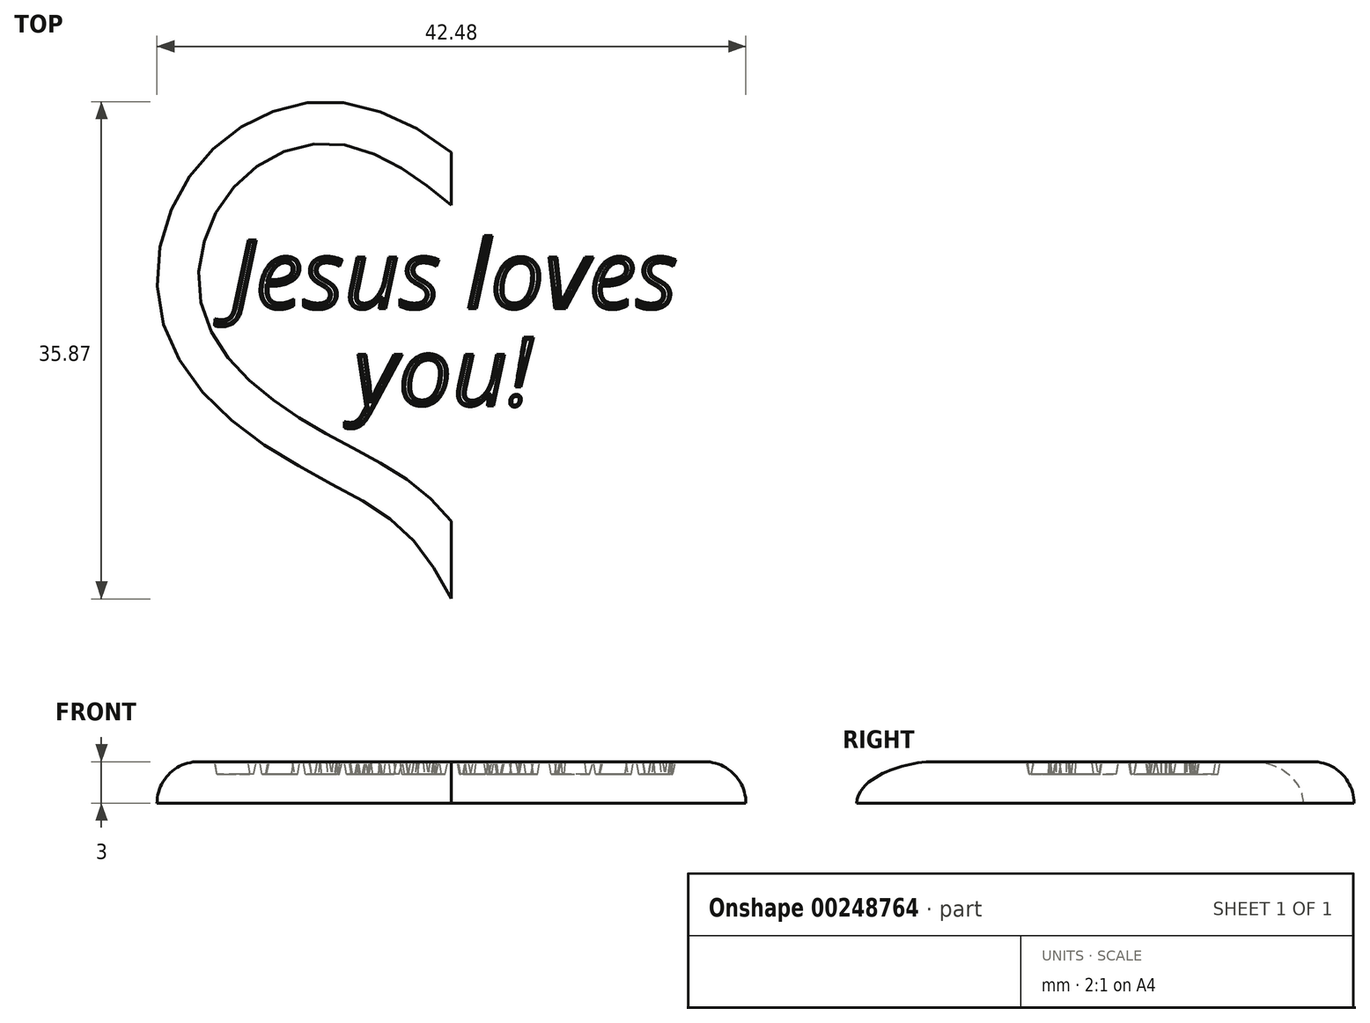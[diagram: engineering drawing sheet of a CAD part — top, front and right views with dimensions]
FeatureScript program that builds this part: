
annotation { "Feature Type Name" : "Feature", "Feature Type Description" : "" }
export const myFeature = defineFeature(function(context is Context, id is Id, definition is map)
    precondition{}
    {
        {
            var Q0;
            Q0=qCreatedBy(makeId("Top.planeOp"),FACE);
            var sketch = newSketch(context, id + "F0", { "sketchPlane" : qUnion([Q0])});
            skText(sketch, "E0", { "text": "Jesus loves", "fontName": "OpenSans-Italic.ttf"});
            skText(sketch, "E1", { "text": "you!", "fontName": "OpenSans-Italic.ttf"});
            const initialGuessF0  = {"E0": [-0.016, 0, 1, 0, 0.005], "E1": [-0.00706, -0.007, 1, 0, 0.005]};
            skSetInitialGuess(sketch, initialGuessF0);
            skSolve(sketch);
        }
        {
            var Q0;
            Q0=qCreatedBy(makeId("Top.planeOp"),FACE);
            var sketch = newSketch(context, id + "F1", { "sketchPlane" : qUnion([Q0])});
            skFitSpline(sketch, "E2", {"points": [v(0, 11.29) * mm, v(-8, 14.88) * mm, v(-14.74, 13.36) * mm, v(-19.74, 8.14) * mm, v(-21.05, 0) * mm, v(-16.7, -7.3) * mm, v(-9.3, -12.3) * mm, v(-3.76, -15.7) * mm, v(0, -20.93) * mm], "startDerivative": vector(-55.24, 43.47) * mm, "endDerivative": vector(28.6, -53.9) * mm});
            skLineSegment(sketch, "E3", {"start": v(0, 11.29) * mm, "end": v(0, -20.93) * mm});
            skSolve(sketch);
        }
        {
            var Q0;
            Q0 = qSketchRegion(id + "F1", true);
            extrude(context, id + "F2", {"entities" : qUnion([Q0]), "oppositeDirection" : true, "depth" : 3 * mm});
        }
        {
            var Q0;
            Q0=makeQuery(id+"F2.opExtrude","SWEPT_BODY",BODY,{"disambiguationData":[OSD([sQuery(id+"F1.wireOp",EDGE,"E2"),sQuery(id+"F1.wireOp",EDGE,"E3")])]});
            var Q1;
            Q1=qCreatedBy(makeId("Right.planeOp"),FACE);
            mirror(context, id + "F3", {"operationType" : NewBodyOperationType.ADD, "entities" : qUnion([Q0]), "mirrorPlane" : qUnion([Q1])});
        }
        {
            var Q0;
            Q0 = qSketchRegion(id + "F0", true);
            extrude(context, id + "F4", {"entities" : qUnion([Q0]), "operationType" : NewBodyOperationType.REMOVE, "oppositeDirection" : true, "depth" : 0.9 * mm, "hasDraft" : true, "draftAngle" : 10 * degree, "draftPullDirection" : true});
        }
        {
            var Q0;
            Q0=makeQuery(id+"F2.opExtrude","CAP_EDGE",EDGE,{"disambiguationData":[OSD([sQuery(id+"F1.wireOp",EDGE,"E2")])],"isStart":true});
            var Q1;
            Q1=makeQuery(id+"F3.opPattern","COPY",EDGE,{"derivedFrom":makeQuery(id+"F2.opExtrude","CAP_EDGE",EDGE,{"disambiguationData":[OSD([sQuery(id+"F1.wireOp",EDGE,"E2")])],"isStart":true}),"instanceName":"1"});
            fillet(context, id + "F5", {"entities" : qUnion([Q0, Q1]), "radius" : 3 * mm, "tangentPropagation" : true, "allowEdgeOverflow" : false});
        }
    });
